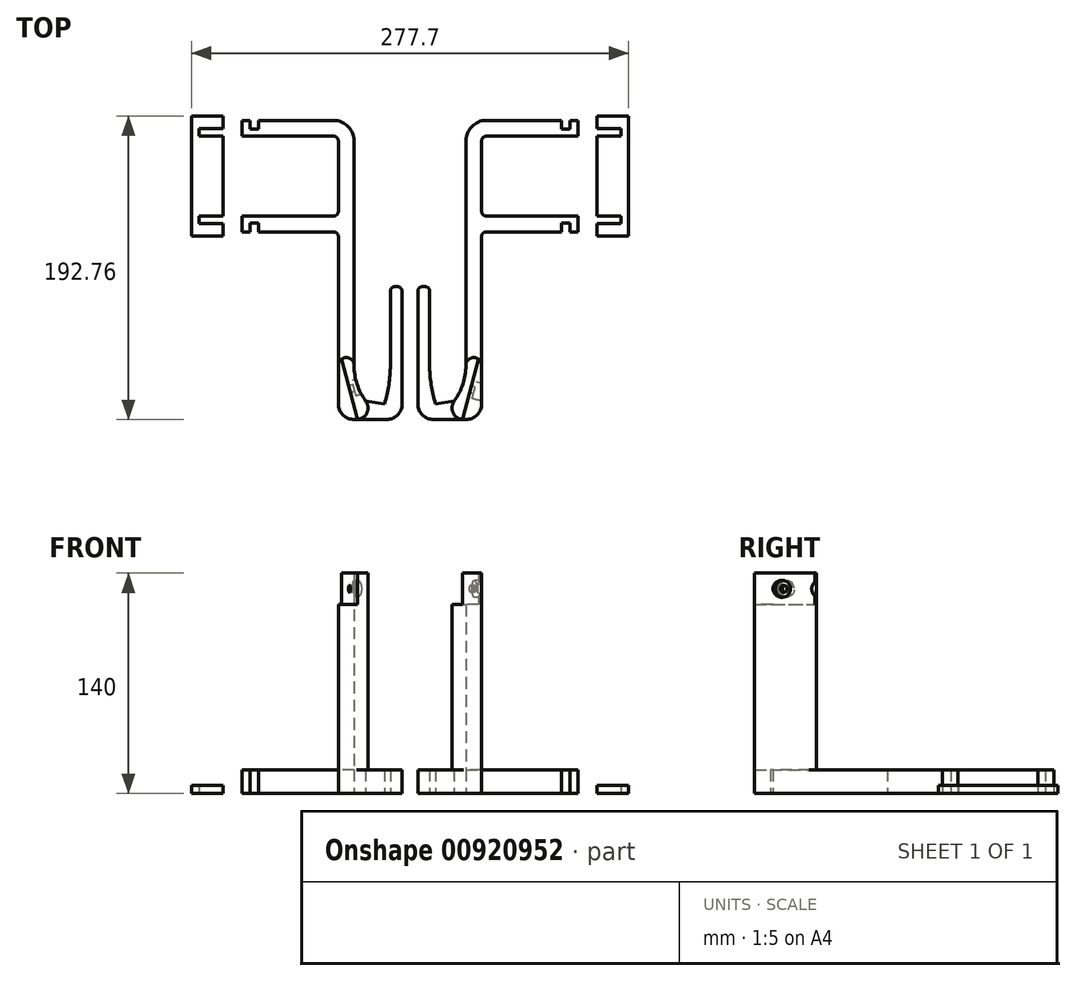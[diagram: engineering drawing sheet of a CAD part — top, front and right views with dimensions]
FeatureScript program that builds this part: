
annotation { "Feature Type Name" : "Feature", "Feature Type Description" : "" }
export const myFeature = defineFeature(function(context is Context, id is Id, definition is map)
    precondition{}
    {
        {
            var Q0;
            Q0=qCreatedBy(makeId("Top.planeOp"),FACE);
            var sketch = newSketch(context, id + "F0", { "sketchPlane" : qUnion([Q0])});
            skLineSegment(sketch, "E0", {"start": v(-83.35, 58.36) * mm, "end": v(-103.35, 58.36) * mm});
            skLineSegment(sketch, "E1", {"start": v(-103.35, 58.36) * mm, "end": v(-103.35, -17.79) * mm});
            skLineSegment(sketch, "E2", {"start": v(-103.35, -17.79) * mm, "end": v(-83.35, -17.79) * mm});
            skLineSegment(sketch, "E3", {"start": v(-83.35, -17.79) * mm, "end": v(-83.35, -9.79) * mm});
            skLineSegment(sketch, "E4", {"start": v(-83.35, -9.79) * mm, "end": v(-98.35, -9.79) * mm});
            skLineSegment(sketch, "E5", {"start": v(-98.35, -9.79) * mm, "end": v(-98.35, -5.09) * mm});
            skLineSegment(sketch, "E6", {"start": v(-98.35, -5.09) * mm, "end": v(-83.35, -5.09) * mm});
            skLineSegment(sketch, "E7", {"start": v(-83.35, -5.09) * mm, "end": v(-83.35, 45.66) * mm});
            skLineSegment(sketch, "E8", {"start": v(-83.35, 45.66) * mm, "end": v(-98.35, 45.66) * mm});
            skLineSegment(sketch, "E9", {"start": v(-98.35, 45.66) * mm, "end": v(-98.35, 50.36) * mm});
            skLineSegment(sketch, "E10", {"start": v(-98.35, 50.36) * mm, "end": v(-83.35, 50.36) * mm});
            skLineSegment(sketch, "E11", {"start": v(-83.35, 50.36) * mm, "end": v(-83.35, 58.36) * mm});
            skSolve(sketch);
        }
        {
            var Q0;
            Q0=makeQuery(id+"F0.imprint","IMPRINT",FACE,{"disambiguationData":[TD([[makeQuery(id+"F0.imprint","IMPRINT",EDGE,{"derivedFrom":sQuery(id+"F0.wireOp",EDGE,"E0")}),1.0]])]});
            extrude(context, id + "F1", {"entities" : qUnion([Q0]), "depth" : 5 * mm, "offsetDistance" : 25 * mm});
        }
        {
            var Q0;
            Q0=qCreatedBy(makeId("Top.planeOp"),FACE);
            var sketch = newSketch(context, id + "F2", { "sketchPlane" : qUnion([Q0])});
            skLineSegment(sketch, "E12", {"start": v(-60.75, 55.6) * mm, "end": v(-13, 55.6) * mm});
            skLineSegment(sketch, "E13", {"start": v(0, 42.6) * mm, "end": v(0, -100) * mm});
            skLineSegment(sketch, "E14", {"start": v(23, -100) * mm, "end": v(23, -53) * mm});
            skLineSegment(sketch, "E15", {"start": v(26, -50) * mm, "end": v(27.5, -50) * mm});
            skLineSegment(sketch, "E16", {"start": v(30.5, -53) * mm, "end": v(30.5, -124.4) * mm});
            skLineSegment(sketch, "E17", {"start": v(20.5, -134.4) * mm, "end": v(0, -134.4) * mm});
            skLineSegment(sketch, "E18", {"start": v(-13, 45.6) * mm, "end": v(-71.15, 45.6) * mm});
            skLineSegment(sketch, "E19", {"start": v(7.4, -122.73) * mm, "end": v(19.3, -124.4) * mm});
            skArc(sketch, "E20", {"start": v(23, -100) * mm, "mid": v(22.07, -112.34) * mm, "end": v(19.3, -124.4) * mm});
            skArc(sketch, "E21", {"start": v(0, -100) * mm, "mid": v(1.9, -111.95) * mm, "end": v(7.4, -122.73) * mm});
            skLineSegment(sketch, "E22", {"start": v(0, -126.51) * mm, "end": v(22.98, -126.51) * mm, "construction": true});
            skLineSegment(sketch, "E23", {"start": v(-71.15, 55.6) * mm, "end": v(-71.15, 45.6) * mm});
            skLineSegment(sketch, "E24", {"start": v(-71.15, 55.6) * mm, "end": v(-66.15, 55.6) * mm});
            skLineSegment(sketch, "E25", {"start": v(-66.15, 55.6) * mm, "end": v(-66.15, 50.2) * mm});
            skLineSegment(sketch, "E26", {"start": v(-66.15, 50.2) * mm, "end": v(-60.75, 50.2) * mm});
            skLineSegment(sketch, "E27", {"start": v(-60.75, 50.2) * mm, "end": v(-60.75, 55.6) * mm});
            skLineSegment(sketch, "E28", {"start": v(-10, 42.6) * mm, "end": v(-10, -2.15) * mm});
            skLineSegment(sketch, "E29", {"start": v(-13, -5.15) * mm, "end": v(-71.15, -5.15) * mm});
            skLineSegment(sketch, "E30", {"start": v(-71.15, -5.15) * mm, "end": v(-71.15, -15.15) * mm});
            skLineSegment(sketch, "E31", {"start": v(-71.15, -15.15) * mm, "end": v(-66.15, -15.15) * mm});
            skLineSegment(sketch, "E32", {"start": v(-66.15, -15.15) * mm, "end": v(-66.15, -9.75) * mm});
            skLineSegment(sketch, "E33", {"start": v(-66.15, -9.75) * mm, "end": v(-60.75, -9.75) * mm});
            skLineSegment(sketch, "E34", {"start": v(-60.75, -9.75) * mm, "end": v(-60.75, -15.15) * mm});
            skLineSegment(sketch, "E35", {"start": v(-60.75, -15.15) * mm, "end": v(-13, -15.15) * mm});
            skLineSegment(sketch, "E36", {"start": v(-10, -18.15) * mm, "end": v(-10, -124.4) * mm});
            skPoint(sketch, "E37.visualSharp", {"position": v(-10, -134.4) * mm});
            skArc(sketch, "E37.filletArc", {"start": v(-10, -124.4) * mm, "mid": v(-7.07, -131.48) * mm, "end": v(0, -134.4) * mm});
            skPoint(sketch, "E38.visualSharp", {"position": v(-10, -5.15) * mm});
            skArc(sketch, "E38.filletArc", {"start": v(-13, -5.15) * mm, "mid": v(-10.88, -4.28) * mm, "end": v(-10, -2.15) * mm});
            skPoint(sketch, "E39.visualSharp", {"position": v(-10, 45.6) * mm});
            skArc(sketch, "E39.filletArc", {"start": v(-10, 42.6) * mm, "mid": v(-10.88, 44.72) * mm, "end": v(-13, 45.6) * mm});
            skPoint(sketch, "E40.visualSharp", {"position": v(-10, -15.15) * mm});
            skArc(sketch, "E40.filletArc", {"start": v(-10, -18.15) * mm, "mid": v(-10.88, -16.03) * mm, "end": v(-13, -15.15) * mm});
            skPoint(sketch, "E41.visualSharp", {"position": v(0, 55.6) * mm});
            skArc(sketch, "E41.filletArc", {"start": v(0, 42.6) * mm, "mid": v(-3.8, 51.79) * mm, "end": v(-13, 55.6) * mm});
            skPoint(sketch, "E42.visualSharp", {"position": v(23, -50) * mm});
            skArc(sketch, "E42.filletArc", {"start": v(26, -50) * mm, "mid": v(23.88, -50.88) * mm, "end": v(23, -53) * mm});
            skPoint(sketch, "E43.visualSharp", {"position": v(30.5, -50) * mm});
            skArc(sketch, "E43.filletArc", {"start": v(30.5, -53) * mm, "mid": v(29.62, -50.88) * mm, "end": v(27.5, -50) * mm});
            skPoint(sketch, "E44.visualSharp", {"position": v(30.5, -134.4) * mm});
            skArc(sketch, "E44.filletArc", {"start": v(20.5, -134.4) * mm, "mid": v(27.57, -131.48) * mm, "end": v(30.5, -124.4) * mm});
            skSolve(sketch);
        }
        {
            var Q0;
            Q0=makeQuery(id+"F2.imprint","IMPRINT",FACE,{"disambiguationData":[TD([[makeQuery(id+"F2.imprint","IMPRINT",EDGE,{"derivedFrom":sQuery(id+"F2.wireOp",EDGE,"E12")}),-1.0]])]});
            extrude(context, id + "F3", {"entities" : qUnion([Q0]), "depth" : 15 * mm, "offsetDistance" : 25 * mm});
        }
        {
            var Q0;
            Q0=makeQuery(id+"F3.opExtrude","SWEPT_BODY",BODY,{"disambiguationData":[OSD([sQuery(id+"F2.wireOp",EDGE,"E12"),sQuery(id+"F2.wireOp",EDGE,"E13"),sQuery(id+"F2.wireOp",EDGE,"E14"),sQuery(id+"F2.wireOp",EDGE,"E15"),sQuery(id+"F2.wireOp",EDGE,"E16"),sQuery(id+"F2.wireOp",EDGE,"c1qe7qy9-5hyt-5kve-fSUS-bYk1D2LQrEFX"),sQuery(id+"F2.wireOp",EDGE,"E17"),sQuery(id+"F2.wireOp",EDGE,"E18"),sQuery(id+"F2.wireOp",EDGE,"E19"),sQuery(id+"F2.wireOp",EDGE,"E20"),sQuery(id+"F2.wireOp",EDGE,"E21"),sQuery(id+"F2.wireOp",EDGE,"E23"),sQuery(id+"F2.wireOp",EDGE,"E24"),sQuery(id+"F2.wireOp",EDGE,"E25"),sQuery(id+"F2.wireOp",EDGE,"E26"),sQuery(id+"F2.wireOp",EDGE,"E27"),sQuery(id+"F2.wireOp",EDGE,"E28"),sQuery(id+"F2.wireOp",EDGE,"E29"),sQuery(id+"F2.wireOp",EDGE,"E30"),sQuery(id+"F2.wireOp",EDGE,"E31"),sQuery(id+"F2.wireOp",EDGE,"E32"),sQuery(id+"F2.wireOp",EDGE,"E33"),sQuery(id+"F2.wireOp",EDGE,"E34"),sQuery(id+"F2.wireOp",EDGE,"E35"),sQuery(id+"F2.wireOp",EDGE,"E36"),sQuery(id+"F2.wireOp",EDGE,"E37.filletArc"),sQuery(id+"F2.wireOp",EDGE,"29bb3225-3ae2-4ab4-8250-15c4004f1066.filletArc"),sQuery(id+"F2.wireOp",EDGE,"E38.filletArc"),sQuery(id+"F2.wireOp",EDGE,"E39.filletArc"),sQuery(id+"F2.wireOp",EDGE,"E40.filletArc"),sQuery(id+"F2.wireOp",EDGE,"E41.filletArc"),sQuery(id+"F2.wireOp",EDGE,"E42.filletArc"),sQuery(id+"F2.wireOp",EDGE,"E43.filletArc")])]});
            var Q1;
            Q1=makeQuery(id+"F1.opExtrude","SWEPT_BODY",BODY,{"disambiguationData":[OSD([sQuery(id+"F0.wireOp",EDGE,"E0"),sQuery(id+"F0.wireOp",EDGE,"E1"),sQuery(id+"F0.wireOp",EDGE,"E2"),sQuery(id+"F0.wireOp",EDGE,"E3"),sQuery(id+"F0.wireOp",EDGE,"E4"),sQuery(id+"F0.wireOp",EDGE,"E5"),sQuery(id+"F0.wireOp",EDGE,"E6"),sQuery(id+"F0.wireOp",EDGE,"E7"),sQuery(id+"F0.wireOp",EDGE,"E8"),sQuery(id+"F0.wireOp",EDGE,"E9"),sQuery(id+"F0.wireOp",EDGE,"E10"),sQuery(id+"F0.wireOp",EDGE,"E11")])]});
            var Q2;
            Q2=makeQuery(id+"F3.opExtrude","SWEPT_FACE",FACE,{"disambiguationData":[OSD([sQuery(id+"F2.wireOp",EDGE,"E16")])]});
            mirror(context, id + "F4", {"entities" : qUnion([Q0, Q1]), "mirrorPlane" : qUnion([Q2])});
        }
        {
            var Q0;
            Q0=makeQuery(id+"F4.opPattern","COPY",BODY,{"derivedFrom":makeQuery(id+"F3.opExtrude","SWEPT_BODY",BODY,{"disambiguationData":[OSD([sQuery(id+"F2.wireOp",EDGE,"E12"),sQuery(id+"F2.wireOp",EDGE,"E13"),sQuery(id+"F2.wireOp",EDGE,"E14"),sQuery(id+"F2.wireOp",EDGE,"E15"),sQuery(id+"F2.wireOp",EDGE,"E16"),sQuery(id+"F2.wireOp",EDGE,"c1qe7qy9-5hyt-5kve-fSUS-bYk1D2LQrEFX"),sQuery(id+"F2.wireOp",EDGE,"E17"),sQuery(id+"F2.wireOp",EDGE,"E18"),sQuery(id+"F2.wireOp",EDGE,"E19"),sQuery(id+"F2.wireOp",EDGE,"E20"),sQuery(id+"F2.wireOp",EDGE,"E21"),sQuery(id+"F2.wireOp",EDGE,"E23"),sQuery(id+"F2.wireOp",EDGE,"E24"),sQuery(id+"F2.wireOp",EDGE,"E25"),sQuery(id+"F2.wireOp",EDGE,"E26"),sQuery(id+"F2.wireOp",EDGE,"E27"),sQuery(id+"F2.wireOp",EDGE,"E28"),sQuery(id+"F2.wireOp",EDGE,"E29"),sQuery(id+"F2.wireOp",EDGE,"E30"),sQuery(id+"F2.wireOp",EDGE,"E31"),sQuery(id+"F2.wireOp",EDGE,"E32"),sQuery(id+"F2.wireOp",EDGE,"E33"),sQuery(id+"F2.wireOp",EDGE,"E34"),sQuery(id+"F2.wireOp",EDGE,"E35"),sQuery(id+"F2.wireOp",EDGE,"E36"),sQuery(id+"F2.wireOp",EDGE,"E37.filletArc"),sQuery(id+"F2.wireOp",EDGE,"29bb3225-3ae2-4ab4-8250-15c4004f1066.filletArc"),sQuery(id+"F2.wireOp",EDGE,"E38.filletArc"),sQuery(id+"F2.wireOp",EDGE,"E39.filletArc"),sQuery(id+"F2.wireOp",EDGE,"E40.filletArc"),sQuery(id+"F2.wireOp",EDGE,"E41.filletArc"),sQuery(id+"F2.wireOp",EDGE,"E42.filletArc"),sQuery(id+"F2.wireOp",EDGE,"E43.filletArc")])]}),"instanceName":"1"});
            var Q1;
            Q1=makeQuery(id+"F4.opPattern","COPY",BODY,{"derivedFrom":makeQuery(id+"F1.opExtrude","SWEPT_BODY",BODY,{"disambiguationData":[OSD([sQuery(id+"F0.wireOp",EDGE,"E0"),sQuery(id+"F0.wireOp",EDGE,"E1"),sQuery(id+"F0.wireOp",EDGE,"E2"),sQuery(id+"F0.wireOp",EDGE,"E3"),sQuery(id+"F0.wireOp",EDGE,"E4"),sQuery(id+"F0.wireOp",EDGE,"E5"),sQuery(id+"F0.wireOp",EDGE,"E6"),sQuery(id+"F0.wireOp",EDGE,"E7"),sQuery(id+"F0.wireOp",EDGE,"E8"),sQuery(id+"F0.wireOp",EDGE,"E9"),sQuery(id+"F0.wireOp",EDGE,"E10"),sQuery(id+"F0.wireOp",EDGE,"E11")])]}),"instanceName":"1"});
            var Q2;
            Q2=makeQuery(id+"F4.opPattern","COPY",EDGE,{"derivedFrom":makeQuery(id+"F3.opExtrude","CAP_EDGE",EDGE,{"disambiguationData":[OSD([sQuery(id+"F2.wireOp",EDGE,"E29")])],"isStart":false}),"instanceName":"1"});
            var Q3;
            Q3=makeQuery(id+"F4.opPattern","COPY",EDGE,{"derivedFrom":makeQuery(id+"F3.opExtrude","CAP_EDGE",EDGE,{"disambiguationData":[OSD([sQuery(id+"F2.wireOp",EDGE,"E29")])],"isStart":false}),"instanceName":"1"});
            transform(context, id + "F5", {"entities" : qUnion([Q0, Q1]), "transformType" : TransformType.TRANSLATION_DISTANCE, "transformDirection" : qUnion([Q3]), "distance" : 10 * mm, "makeCopy" : false});
        }
        {
            var Q0;
            Q0=makeQuery(id+"F3.opExtrude","CAP_FACE",FACE,{"disambiguationData":[OSD([sQuery(id+"F2.wireOp",EDGE,"E12"),sQuery(id+"F2.wireOp",EDGE,"E13"),sQuery(id+"F2.wireOp",EDGE,"E14"),sQuery(id+"F2.wireOp",EDGE,"E15"),sQuery(id+"F2.wireOp",EDGE,"E16"),sQuery(id+"F2.wireOp",EDGE,"E17"),sQuery(id+"F2.wireOp",EDGE,"E18"),sQuery(id+"F2.wireOp",EDGE,"E19"),sQuery(id+"F2.wireOp",EDGE,"E20"),sQuery(id+"F2.wireOp",EDGE,"E21"),sQuery(id+"F2.wireOp",EDGE,"E23"),sQuery(id+"F2.wireOp",EDGE,"E24"),sQuery(id+"F2.wireOp",EDGE,"E25"),sQuery(id+"F2.wireOp",EDGE,"E26"),sQuery(id+"F2.wireOp",EDGE,"E27"),sQuery(id+"F2.wireOp",EDGE,"E28"),sQuery(id+"F2.wireOp",EDGE,"E29"),sQuery(id+"F2.wireOp",EDGE,"E30"),sQuery(id+"F2.wireOp",EDGE,"E31"),sQuery(id+"F2.wireOp",EDGE,"E32"),sQuery(id+"F2.wireOp",EDGE,"E33"),sQuery(id+"F2.wireOp",EDGE,"E34"),sQuery(id+"F2.wireOp",EDGE,"E35"),sQuery(id+"F2.wireOp",EDGE,"E36"),sQuery(id+"F2.wireOp",EDGE,"E37.filletArc"),sQuery(id+"F2.wireOp",EDGE,"E38.filletArc"),sQuery(id+"F2.wireOp",EDGE,"E39.filletArc"),sQuery(id+"F2.wireOp",EDGE,"E40.filletArc"),sQuery(id+"F2.wireOp",EDGE,"E41.filletArc"),sQuery(id+"F2.wireOp",EDGE,"E42.filletArc"),sQuery(id+"F2.wireOp",EDGE,"E43.filletArc"),sQuery(id+"F2.wireOp",EDGE,"E44.filletArc")])],"isStart":false});
            var sketch = newSketch(context, id + "F6", { "sketchPlane" : qUnion([Q0])});
            skArc(sketch, "E45", {"start": v(0, -100) * mm, "mid": v(-5, -95) * mm, "end": v(-10, -100) * mm});
            skArc(sketch, "E46", {"start": v(1.46, -134.4) * mm, "mid": v(8, -130.39) * mm, "end": v(7.4, -122.73) * mm});
            skSolve(sketch);
        }
        {
            var Q0;
            {var subQ2=sQuery(id+"F6.wireOp",EDGE,"E45");Q0=makeQuery(id+"F6.imprint","IMPRINT",FACE,{"disambiguationData":[TD([[makeQuery(id+"F6.imprint","IMPRINT",EDGE,{"derivedFrom":subQ2}),1.0]])]});}
            extrude(context, id + "F7", {"entities" : qUnion([Q0]), "operationType" : NewBodyOperationType.ADD, "depth" : 125 * mm, "offsetDistance" : 25 * mm});
        }
        {
            var Q0;
            Q0=makeQuery(id+"F4.opPattern","COPY",FACE,{"derivedFrom":makeQuery(id+"F3.opExtrude","CAP_FACE",FACE,{"disambiguationData":[OSD([sQuery(id+"F2.wireOp",EDGE,"E12"),sQuery(id+"F2.wireOp",EDGE,"E13"),sQuery(id+"F2.wireOp",EDGE,"E14"),sQuery(id+"F2.wireOp",EDGE,"E15"),sQuery(id+"F2.wireOp",EDGE,"E16"),sQuery(id+"F2.wireOp",EDGE,"E17"),sQuery(id+"F2.wireOp",EDGE,"E18"),sQuery(id+"F2.wireOp",EDGE,"E19"),sQuery(id+"F2.wireOp",EDGE,"E20"),sQuery(id+"F2.wireOp",EDGE,"E21"),sQuery(id+"F2.wireOp",EDGE,"E23"),sQuery(id+"F2.wireOp",EDGE,"E24"),sQuery(id+"F2.wireOp",EDGE,"E25"),sQuery(id+"F2.wireOp",EDGE,"E26"),sQuery(id+"F2.wireOp",EDGE,"E27"),sQuery(id+"F2.wireOp",EDGE,"E28"),sQuery(id+"F2.wireOp",EDGE,"E29"),sQuery(id+"F2.wireOp",EDGE,"E30"),sQuery(id+"F2.wireOp",EDGE,"E31"),sQuery(id+"F2.wireOp",EDGE,"E32"),sQuery(id+"F2.wireOp",EDGE,"E33"),sQuery(id+"F2.wireOp",EDGE,"E34"),sQuery(id+"F2.wireOp",EDGE,"E35"),sQuery(id+"F2.wireOp",EDGE,"E36"),sQuery(id+"F2.wireOp",EDGE,"E37.filletArc"),sQuery(id+"F2.wireOp",EDGE,"E38.filletArc"),sQuery(id+"F2.wireOp",EDGE,"E39.filletArc"),sQuery(id+"F2.wireOp",EDGE,"E40.filletArc"),sQuery(id+"F2.wireOp",EDGE,"E41.filletArc"),sQuery(id+"F2.wireOp",EDGE,"E42.filletArc"),sQuery(id+"F2.wireOp",EDGE,"E43.filletArc"),sQuery(id+"F2.wireOp",EDGE,"E44.filletArc")])],"isStart":false}),"instanceName":"1"});
            var sketch = newSketch(context, id + "F8", { "sketchPlane" : qUnion([Q0])});
            skArc(sketch, "E47", {"start": v(81, -100) * mm, "mid": v(76, -95) * mm, "end": v(71, -100) * mm});
            skArc(sketch, "E48", {"start": v(63.6, -122.73) * mm, "mid": v(63, -130.39) * mm, "end": v(69.54, -134.4) * mm});
            skSolve(sketch);
        }
        {
            var Q0;
            {var subQ2=sQuery(id+"F8.wireOp",EDGE,"E47");Q0=makeQuery(id+"F8.imprint","IMPRINT",FACE,{"disambiguationData":[TD([[makeQuery(id+"F8.imprint","IMPRINT",EDGE,{"derivedFrom":subQ2}),1.0]])]});}
            extrude(context, id + "F9", {"entities" : qUnion([Q0]), "operationType" : NewBodyOperationType.ADD, "depth" : 125 * mm, "offsetDistance" : 25 * mm});
        }
        {
            var Q0;
            {var subQ0=sQuery(id+"F2.wireOp",EDGE,"E36");Q0=makeQuery(id+"F9.boolean.opBoolean","MERGE",FACE,{"derivedFrom":[makeQuery(id+"F4.opPattern","COPY",FACE,{"derivedFrom":makeQuery(id+"F3.opExtrude","SWEPT_FACE",FACE,{"disambiguationData":[OSD([subQ0])]}),"instanceName":"1"}),makeQuery(id+"F9.opExtrude","SWEPT_FACE",FACE,{"disambiguationData":[OSD([subQ0])]})]});}
            var sketch = newSketch(context, id + "F10", { "sketchPlane" : qUnion([Q0])});
            skLineSegment(sketch, "E49.bottom", {"start": v(-80, 140) * mm, "end": v(-150, 140) * mm});
            skLineSegment(sketch, "E49.top", {"start": v(-80, 120) * mm, "end": v(-150, 120) * mm});
            skLineSegment(sketch, "E49.left", {"start": v(-80, 140) * mm, "end": v(-80, 120) * mm});
            skLineSegment(sketch, "E49.right", {"start": v(-150, 140) * mm, "end": v(-150, 120) * mm});
            skPoint(sketch, "E50", {"position": v(-115, 140) * mm});
            skPoint(sketch, "E51", {"position": v(-115, 120) * mm});
            skLineSegment(sketch, "E52", {"start": v(-115, 140) * mm, "end": v(-115, 120) * mm, "construction": true});
            skSolve(sketch);
        }
        {
            var Q0;
            {var subQ0=sQuery(id+"F10.wireOp",EDGE,"E49.bottom");var subQ2=sQuery(id+"F2.wireOp",EDGE,"E36");var subQ5=makeQuery(id+"F9.opExtrude","SWEPT_EDGE",EDGE,{"disambiguationData":[OSD([subQ2,sQuery(id+"F8.wireOp",EDGE,"E47")])]});var subQ6=makeQuery(id+"F10.imprint","INTERSECT",VERTEX,{"derivedFrom":[subQ5,subQ0]});Q0=makeQuery(id+"F10.imprint","IMPRINT",FACE,{"disambiguationData":[TD([[makeQuery(id+"F10.imprint","IMPRINT",EDGE,{"disambiguationData":[TD([[subQ6,-1.0]])],"derivedFrom":subQ5}),-1.0]])]});}
            var Q1;
            {var subQ3=sQuery(id+"F10.wireOp",EDGE,"E49.left");Q1=makeQuery(id+"F10.imprint","IMPRINT",FACE,{"disambiguationData":[TD([[makeQuery(id+"F10.imprint","IMPRINT",EDGE,{"derivedFrom":subQ3}),-1.0]])]});}
            var Q2;
            {var subQ5=sQuery(id+"F10.wireOp",EDGE,"E49.right");Q2=makeQuery(id+"F10.imprint","IMPRINT",FACE,{"disambiguationData":[TD([[makeQuery(id+"F10.imprint","IMPRINT",EDGE,{"derivedFrom":subQ5}),1.0]])]});}
            extrude(context, id + "F11", {"entities" : qUnion([Q0, Q1, Q2]), "oppositeDirection" : true, "depth" : 15 * mm, "offsetDistance" : 25 * mm});
        }
        {
            var Q0;
            Q0=makeQuery(id+"F11.opExtrude","SWEPT_BODY",BODY,{"disambiguationData":[OSD([sQuery(id+"F10.wireOp",EDGE,"E49.bottom"),sQuery(id+"F10.wireOp",EDGE,"E49.top"),sQuery(id+"F10.wireOp",EDGE,"E49.left"),sQuery(id+"F10.wireOp",EDGE,"E49.right")])]});
            var Q1;
            Q1=sQuery(id+"F10.wireOp",EDGE,"E52");
            transform(context, id + "F12", {"entities" : qUnion([Q0]), "transformType" : TransformType.ROTATION, "transformAxis" : qUnion([Q1]), "angle" : 15 * degree, "makeCopy" : false});
        }
        {
            var Q0;
            Q0=makeQuery(id+"F11.opExtrude","SWEPT_BODY",BODY,{"disambiguationData":[OSD([sQuery(id+"F10.wireOp",EDGE,"E49.bottom"),sQuery(id+"F10.wireOp",EDGE,"E49.top"),sQuery(id+"F10.wireOp",EDGE,"E49.left"),sQuery(id+"F10.wireOp",EDGE,"E49.right")])]});
            var Q1;
            Q1=makeQuery(id+"F4.opPattern","COPY",EDGE,{"derivedFrom":makeQuery(id+"F3.opExtrude","CAP_EDGE",EDGE,{"disambiguationData":[OSD([sQuery(id+"F2.wireOp",EDGE,"E17")])],"isStart":false}),"instanceName":"1"});
            transform(context, id + "F13", {"entities" : qUnion([Q0]), "transformType" : TransformType.TRANSLATION_DISTANCE, "transformDirection" : qUnion([Q1]), "distance" : 7 * mm, "oppositeDirection" : true, "makeCopy" : false});
        }
        {
            var Q0;
            Q0=makeQuery(id+"F11.opExtrude","SWEPT_BODY",BODY,{"disambiguationData":[OSD([sQuery(id+"F10.wireOp",EDGE,"E49.bottom"),sQuery(id+"F10.wireOp",EDGE,"E49.top"),sQuery(id+"F10.wireOp",EDGE,"E49.left"),sQuery(id+"F10.wireOp",EDGE,"E49.right")])]});
            var Q1;
            Q1=makeQuery(id+"F4.opPattern","COPY",BODY,{"derivedFrom":makeQuery(id+"F3.opExtrude","SWEPT_BODY",BODY,{"disambiguationData":[OSD([sQuery(id+"F2.wireOp",EDGE,"E12"),sQuery(id+"F2.wireOp",EDGE,"E13"),sQuery(id+"F2.wireOp",EDGE,"E14"),sQuery(id+"F2.wireOp",EDGE,"E15"),sQuery(id+"F2.wireOp",EDGE,"E16"),sQuery(id+"F2.wireOp",EDGE,"E17"),sQuery(id+"F2.wireOp",EDGE,"E18"),sQuery(id+"F2.wireOp",EDGE,"E19"),sQuery(id+"F2.wireOp",EDGE,"E20"),sQuery(id+"F2.wireOp",EDGE,"E21"),sQuery(id+"F2.wireOp",EDGE,"E23"),sQuery(id+"F2.wireOp",EDGE,"E24"),sQuery(id+"F2.wireOp",EDGE,"E25"),sQuery(id+"F2.wireOp",EDGE,"E26"),sQuery(id+"F2.wireOp",EDGE,"E27"),sQuery(id+"F2.wireOp",EDGE,"E28"),sQuery(id+"F2.wireOp",EDGE,"E29"),sQuery(id+"F2.wireOp",EDGE,"E30"),sQuery(id+"F2.wireOp",EDGE,"E31"),sQuery(id+"F2.wireOp",EDGE,"E32"),sQuery(id+"F2.wireOp",EDGE,"E33"),sQuery(id+"F2.wireOp",EDGE,"E34"),sQuery(id+"F2.wireOp",EDGE,"E35"),sQuery(id+"F2.wireOp",EDGE,"E36"),sQuery(id+"F2.wireOp",EDGE,"E37.filletArc"),sQuery(id+"F2.wireOp",EDGE,"E38.filletArc"),sQuery(id+"F2.wireOp",EDGE,"E39.filletArc"),sQuery(id+"F2.wireOp",EDGE,"E40.filletArc"),sQuery(id+"F2.wireOp",EDGE,"E41.filletArc"),sQuery(id+"F2.wireOp",EDGE,"E42.filletArc"),sQuery(id+"F2.wireOp",EDGE,"E43.filletArc"),sQuery(id+"F2.wireOp",EDGE,"E44.filletArc")])]}),"instanceName":"1"});
            booleanBodies(context, id + "F14", {"operationType" : BooleanOperationType.SUBTRACTION, "tools" : qUnion([Q0]), "targets" : qUnion([Q1])});
        }
        {
            var Q0;
            {var subQ0=sQuery(id+"F2.wireOp",EDGE,"E36");Q0=makeQuery(id+"F7.boolean.opBoolean","MERGE",FACE,{"derivedFrom":[makeQuery(id+"F3.opExtrude","SWEPT_FACE",FACE,{"disambiguationData":[OSD([subQ0])]}),makeQuery(id+"F7.opExtrude","SWEPT_FACE",FACE,{"disambiguationData":[OSD([subQ0])]})]});}
            var sketch = newSketch(context, id + "F15", { "sketchPlane" : qUnion([Q0])});
            skLineSegment(sketch, "E53.bottom", {"start": v(150, 140) * mm, "end": v(80, 140) * mm});
            skLineSegment(sketch, "E53.top", {"start": v(150, 120) * mm, "end": v(80, 120) * mm});
            skLineSegment(sketch, "E53.left", {"start": v(150, 140) * mm, "end": v(150, 120) * mm});
            skLineSegment(sketch, "E53.right", {"start": v(80, 140) * mm, "end": v(80, 120) * mm});
            skPoint(sketch, "E54", {"position": v(115, 140) * mm});
            skPoint(sketch, "E55", {"position": v(115, 120) * mm});
            skLineSegment(sketch, "E56", {"start": v(115, 140) * mm, "end": v(115, 120) * mm, "construction": true});
            skSolve(sketch);
        }
        {
            var Q0;
            {var subQ0=sQuery(id+"F15.wireOp",EDGE,"E53.bottom");var subQ2=sQuery(id+"F2.wireOp",EDGE,"E36");var subQ5=makeQuery(id+"F7.opExtrude","SWEPT_EDGE",EDGE,{"disambiguationData":[OSD([subQ2,sQuery(id+"F6.wireOp",EDGE,"E45")])]});var subQ6=makeQuery(id+"F15.imprint","INTERSECT",VERTEX,{"derivedFrom":[subQ5,subQ0]});Q0=makeQuery(id+"F15.imprint","IMPRINT",FACE,{"disambiguationData":[TD([[makeQuery(id+"F15.imprint","IMPRINT",EDGE,{"disambiguationData":[TD([[subQ6,-1.0]])],"derivedFrom":subQ5}),1.0]])]});}
            var Q1;
            {var subQ3=sQuery(id+"F15.wireOp",EDGE,"E53.right");Q1=makeQuery(id+"F15.imprint","IMPRINT",FACE,{"disambiguationData":[TD([[makeQuery(id+"F15.imprint","IMPRINT",EDGE,{"derivedFrom":subQ3}),1.0]])]});}
            var Q2;
            {var subQ5=sQuery(id+"F15.wireOp",EDGE,"E53.left");Q2=makeQuery(id+"F15.imprint","IMPRINT",FACE,{"disambiguationData":[TD([[makeQuery(id+"F15.imprint","IMPRINT",EDGE,{"derivedFrom":subQ5}),-1.0]])]});}
            extrude(context, id + "F16", {"entities" : qUnion([Q0, Q1, Q2]), "depth" : 15 * mm, "offsetDistance" : 25 * mm});
        }
        {
            var Q0;
            Q0=makeQuery(id+"F16.opExtrude","SWEPT_BODY",BODY,{"disambiguationData":[OSD([sQuery(id+"F15.wireOp",EDGE,"E53.bottom"),sQuery(id+"F15.wireOp",EDGE,"E53.top"),sQuery(id+"F15.wireOp",EDGE,"E53.left"),sQuery(id+"F15.wireOp",EDGE,"E53.right")])]});
            var Q1;
            Q1=sQuery(id+"F15.wireOp",EDGE,"E56");
            transform(context, id + "F17", {"entities" : qUnion([Q0]), "transformType" : TransformType.ROTATION, "transformAxis" : qUnion([Q1]), "angle" : 15 * degree, "oppositeDirection" : true, "makeCopy" : false});
        }
        {
            var Q0;
            Q0=makeQuery(id+"F16.opExtrude","SWEPT_BODY",BODY,{"disambiguationData":[OSD([sQuery(id+"F15.wireOp",EDGE,"E53.bottom"),sQuery(id+"F15.wireOp",EDGE,"E53.top"),sQuery(id+"F15.wireOp",EDGE,"E53.left"),sQuery(id+"F15.wireOp",EDGE,"E53.right")])]});
            var Q1;
            Q1=makeQuery(id+"F3.opExtrude","CAP_EDGE",EDGE,{"disambiguationData":[OSD([sQuery(id+"F2.wireOp",EDGE,"E17")])],"isStart":false});
            transform(context, id + "F18", {"entities" : qUnion([Q0]), "transformType" : TransformType.TRANSLATION_DISTANCE, "transformDirection" : qUnion([Q1]), "distance" : 7 * mm, "oppositeDirection" : true, "makeCopy" : false});
        }
        {
            var Q0;
            Q0=makeQuery(id+"F16.opExtrude","SWEPT_BODY",BODY,{"disambiguationData":[OSD([sQuery(id+"F15.wireOp",EDGE,"E53.bottom"),sQuery(id+"F15.wireOp",EDGE,"E53.top"),sQuery(id+"F15.wireOp",EDGE,"E53.left"),sQuery(id+"F15.wireOp",EDGE,"E53.right")])]});
            var Q1;
            Q1=makeQuery(id+"F3.opExtrude","SWEPT_BODY",BODY,{"disambiguationData":[OSD([sQuery(id+"F2.wireOp",EDGE,"E12"),sQuery(id+"F2.wireOp",EDGE,"E13"),sQuery(id+"F2.wireOp",EDGE,"E14"),sQuery(id+"F2.wireOp",EDGE,"E15"),sQuery(id+"F2.wireOp",EDGE,"E16"),sQuery(id+"F2.wireOp",EDGE,"E17"),sQuery(id+"F2.wireOp",EDGE,"E18"),sQuery(id+"F2.wireOp",EDGE,"E19"),sQuery(id+"F2.wireOp",EDGE,"E20"),sQuery(id+"F2.wireOp",EDGE,"E21"),sQuery(id+"F2.wireOp",EDGE,"E23"),sQuery(id+"F2.wireOp",EDGE,"E24"),sQuery(id+"F2.wireOp",EDGE,"E25"),sQuery(id+"F2.wireOp",EDGE,"E26"),sQuery(id+"F2.wireOp",EDGE,"E27"),sQuery(id+"F2.wireOp",EDGE,"E28"),sQuery(id+"F2.wireOp",EDGE,"E29"),sQuery(id+"F2.wireOp",EDGE,"E30"),sQuery(id+"F2.wireOp",EDGE,"E31"),sQuery(id+"F2.wireOp",EDGE,"E32"),sQuery(id+"F2.wireOp",EDGE,"E33"),sQuery(id+"F2.wireOp",EDGE,"E34"),sQuery(id+"F2.wireOp",EDGE,"E35"),sQuery(id+"F2.wireOp",EDGE,"E36"),sQuery(id+"F2.wireOp",EDGE,"E37.filletArc"),sQuery(id+"F2.wireOp",EDGE,"E38.filletArc"),sQuery(id+"F2.wireOp",EDGE,"E39.filletArc"),sQuery(id+"F2.wireOp",EDGE,"E40.filletArc"),sQuery(id+"F2.wireOp",EDGE,"E41.filletArc"),sQuery(id+"F2.wireOp",EDGE,"E42.filletArc"),sQuery(id+"F2.wireOp",EDGE,"E43.filletArc"),sQuery(id+"F2.wireOp",EDGE,"E44.filletArc")])]});
            booleanBodies(context, id + "F19", {"operationType" : BooleanOperationType.SUBTRACTION, "tools" : qUnion([Q0]), "targets" : qUnion([Q1])});
        }
        {
            var Q0;
            Q0=makeQuery(id+"F14.opBoolean","COPY",FACE,{"derivedFrom":makeQuery(id+"F11.opExtrude","CAP_FACE",FACE,{"disambiguationData":[OSD([sQuery(id+"F10.wireOp",EDGE,"E49.bottom"),sQuery(id+"F10.wireOp",EDGE,"E49.top"),sQuery(id+"F10.wireOp",EDGE,"E49.left"),sQuery(id+"F10.wireOp",EDGE,"E49.right")])],"isStart":true})});
            var sketch = newSketch(context, id + "F20", { "sketchPlane" : qUnion([Q0])});
            skLineSegment(sketch, "E57", {"start": v(92.15, 120) * mm, "end": v(92.15, 140) * mm, "construction": true});
            skLineSegment(sketch, "E58", {"start": v(72.32, 130) * mm, "end": v(111.98, 130) * mm, "construction": true});
            skPoint(sketch, "E59", {"position": v(92.15, 130) * mm});
            skCircle(sketch, "E60", {"center": v(92.15, 130) * mm, "radius": 5.4 * mm});
            skSolve(sketch);
        }
        {
            var Q0;
            Q0=sQuery(id+"F20.wireOp",VERTEX,"E59");
            var Q1;
            Q1=makeQuery(id+"F4.opPattern","COPY",BODY,{"derivedFrom":makeQuery(id+"F3.opExtrude","SWEPT_BODY",BODY,{"disambiguationData":[OSD([sQuery(id+"F2.wireOp",EDGE,"E12"),sQuery(id+"F2.wireOp",EDGE,"E13"),sQuery(id+"F2.wireOp",EDGE,"E14"),sQuery(id+"F2.wireOp",EDGE,"E15"),sQuery(id+"F2.wireOp",EDGE,"E16"),sQuery(id+"F2.wireOp",EDGE,"E17"),sQuery(id+"F2.wireOp",EDGE,"E18"),sQuery(id+"F2.wireOp",EDGE,"E19"),sQuery(id+"F2.wireOp",EDGE,"E20"),sQuery(id+"F2.wireOp",EDGE,"E21"),sQuery(id+"F2.wireOp",EDGE,"E23"),sQuery(id+"F2.wireOp",EDGE,"E24"),sQuery(id+"F2.wireOp",EDGE,"E25"),sQuery(id+"F2.wireOp",EDGE,"E26"),sQuery(id+"F2.wireOp",EDGE,"E27"),sQuery(id+"F2.wireOp",EDGE,"E28"),sQuery(id+"F2.wireOp",EDGE,"E29"),sQuery(id+"F2.wireOp",EDGE,"E30"),sQuery(id+"F2.wireOp",EDGE,"E31"),sQuery(id+"F2.wireOp",EDGE,"E32"),sQuery(id+"F2.wireOp",EDGE,"E33"),sQuery(id+"F2.wireOp",EDGE,"E34"),sQuery(id+"F2.wireOp",EDGE,"E35"),sQuery(id+"F2.wireOp",EDGE,"E36"),sQuery(id+"F2.wireOp",EDGE,"E37.filletArc"),sQuery(id+"F2.wireOp",EDGE,"E38.filletArc"),sQuery(id+"F2.wireOp",EDGE,"E39.filletArc"),sQuery(id+"F2.wireOp",EDGE,"E40.filletArc"),sQuery(id+"F2.wireOp",EDGE,"E41.filletArc"),sQuery(id+"F2.wireOp",EDGE,"E42.filletArc"),sQuery(id+"F2.wireOp",EDGE,"E43.filletArc"),sQuery(id+"F2.wireOp",EDGE,"E44.filletArc")])]}),"instanceName":"1"});
            hole(context, id + "F21", {"style" : HoleStyle.SIMPLE, "endStyle" : HoleEndStyle.THROUGH, "holeDiameter" : 4.5 * mm, "majorDiameter" : 5 * mm, "isTappedThrough" : true, "tappedDepth" : 12 * mm, "tapClearance" : 3, "locations" : qUnion([Q0]), "scope" : qUnion([Q1])});
        }
        {
            var Q0;
            Q0=makeQuery(id+"F20.imprint","IMPRINT",FACE,{"disambiguationData":[TD([[makeQuery(id+"F20.imprint","IMPRINT",EDGE,{"derivedFrom":sQuery(id+"F20.wireOp",EDGE,"E60")}),1.0]])]});
            extrude(context, id + "F22", {"entities" : qUnion([Q0]), "operationType" : NewBodyOperationType.REMOVE, "endBound" : BoundingType.THROUGH_ALL, "oppositeDirection" : true, "depth" : 10 * mm, "offsetDistance" : 25 * mm, "hasSecondDirection" : true, "secondDirectionOppositeDirection" : true, "secondDirectionDepth" : 2.5 * mm});
        }
        {
            var Q0;
            Q0=makeQuery(id+"F19.opBoolean","COPY",FACE,{"derivedFrom":makeQuery(id+"F16.opExtrude","CAP_FACE",FACE,{"disambiguationData":[OSD([sQuery(id+"F15.wireOp",EDGE,"E53.bottom"),sQuery(id+"F15.wireOp",EDGE,"E53.top"),sQuery(id+"F15.wireOp",EDGE,"E53.left"),sQuery(id+"F15.wireOp",EDGE,"E53.right")])],"isStart":true})});
            var sketch = newSketch(context, id + "F23", { "sketchPlane" : qUnion([Q0])});
            skLineSegment(sketch, "E61", {"start": v(90.7, 130) * mm, "end": v(130.36, 130) * mm, "construction": true});
            skLineSegment(sketch, "E62", {"start": v(110.53, 120) * mm, "end": v(110.53, 140) * mm, "construction": true});
            skPoint(sketch, "E63", {"position": v(110.53, 130) * mm});
            skCircle(sketch, "E64", {"center": v(110.53, 130) * mm, "radius": 5.12 * mm});
            skSolve(sketch);
        }
        {
            var Q0;
            Q0=sQuery(id+"F23.wireOp",VERTEX,"E63");
            var Q1;
            Q1=makeQuery(id+"F3.opExtrude","SWEPT_BODY",BODY,{"disambiguationData":[OSD([sQuery(id+"F2.wireOp",EDGE,"E12"),sQuery(id+"F2.wireOp",EDGE,"E13"),sQuery(id+"F2.wireOp",EDGE,"E14"),sQuery(id+"F2.wireOp",EDGE,"E15"),sQuery(id+"F2.wireOp",EDGE,"E16"),sQuery(id+"F2.wireOp",EDGE,"E17"),sQuery(id+"F2.wireOp",EDGE,"E18"),sQuery(id+"F2.wireOp",EDGE,"E19"),sQuery(id+"F2.wireOp",EDGE,"E20"),sQuery(id+"F2.wireOp",EDGE,"E21"),sQuery(id+"F2.wireOp",EDGE,"E23"),sQuery(id+"F2.wireOp",EDGE,"E24"),sQuery(id+"F2.wireOp",EDGE,"E25"),sQuery(id+"F2.wireOp",EDGE,"E26"),sQuery(id+"F2.wireOp",EDGE,"E27"),sQuery(id+"F2.wireOp",EDGE,"E28"),sQuery(id+"F2.wireOp",EDGE,"E29"),sQuery(id+"F2.wireOp",EDGE,"E30"),sQuery(id+"F2.wireOp",EDGE,"E31"),sQuery(id+"F2.wireOp",EDGE,"E32"),sQuery(id+"F2.wireOp",EDGE,"E33"),sQuery(id+"F2.wireOp",EDGE,"E34"),sQuery(id+"F2.wireOp",EDGE,"E35"),sQuery(id+"F2.wireOp",EDGE,"E36"),sQuery(id+"F2.wireOp",EDGE,"E37.filletArc"),sQuery(id+"F2.wireOp",EDGE,"E38.filletArc"),sQuery(id+"F2.wireOp",EDGE,"E39.filletArc"),sQuery(id+"F2.wireOp",EDGE,"E40.filletArc"),sQuery(id+"F2.wireOp",EDGE,"E41.filletArc"),sQuery(id+"F2.wireOp",EDGE,"E42.filletArc"),sQuery(id+"F2.wireOp",EDGE,"E43.filletArc"),sQuery(id+"F2.wireOp",EDGE,"E44.filletArc")])]});
            hole(context, id + "F24", {"style" : HoleStyle.SIMPLE, "endStyle" : HoleEndStyle.THROUGH, "holeDiameter" : 4.5 * mm, "majorDiameter" : 5 * mm, "isTappedThrough" : true, "tappedDepth" : 12 * mm, "tapClearance" : 3, "locations" : qUnion([Q0]), "scope" : qUnion([Q1])});
        }
        {
            var Q0;
            Q0=makeQuery(id+"F23.imprint","IMPRINT",FACE,{"disambiguationData":[TD([[makeQuery(id+"F23.imprint","IMPRINT",EDGE,{"derivedFrom":sQuery(id+"F23.wireOp",EDGE,"E64")}),1.0]])]});
            extrude(context, id + "F25", {"entities" : qUnion([Q0]), "operationType" : NewBodyOperationType.REMOVE, "endBound" : BoundingType.THROUGH_ALL, "oppositeDirection" : true, "depth" : 25 * mm, "offsetDistance" : 25 * mm, "hasSecondDirection" : true, "secondDirectionOppositeDirection" : true, "secondDirectionDepth" : 3 * mm});
        }
    });
